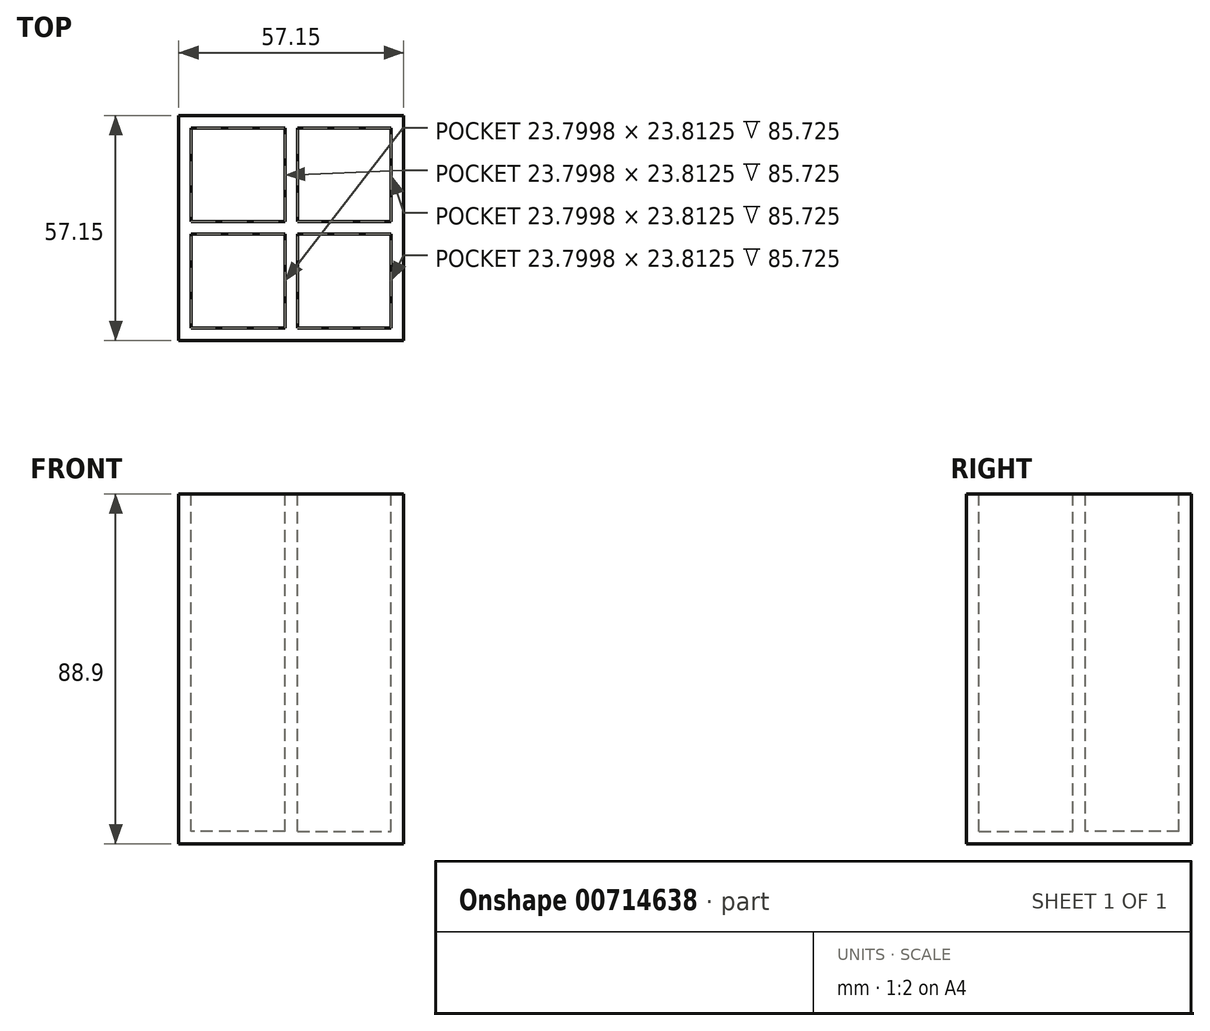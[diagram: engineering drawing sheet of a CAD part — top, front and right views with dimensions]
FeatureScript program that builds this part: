
annotation { "Feature Type Name" : "Feature", "Feature Type Description" : "" }
export const myFeature = defineFeature(function(context is Context, id is Id, definition is map)
    precondition{}
    {
        {
            var Q0;
            Q0=qCreatedBy(makeId("Top.planeOp"),FACE);
            var sketch = newSketch(context, id + "F0", { "sketchPlane" : qUnion([Q0])});
            skLineSegment(sketch, "E0.bottom", {"start": v(-54.12, 72.6) * mm, "end": v(3.03, 72.6) * mm});
            skLineSegment(sketch, "E0.top", {"start": v(-54.12, 15.45) * mm, "end": v(3.03, 15.45) * mm});
            skLineSegment(sketch, "E0.left", {"start": v(-54.12, 72.6) * mm, "end": v(-54.12, 15.45) * mm});
            skLineSegment(sketch, "E0.right", {"start": v(3.03, 72.6) * mm, "end": v(3.03, 15.45) * mm});
            skSolve(sketch);
        }
        {
            var Q0;
            Q0=makeQuery(id+"F0.imprint","IMPRINT",FACE,{"disambiguationData":[TD([[makeQuery(id+"F0.imprint","IMPRINT",EDGE,{"derivedFrom":sQuery(id+"F0.wireOp",EDGE,"E0.bottom")}),-1.0]])]});
            extrude(context, id + "F1", {"entities" : qUnion([Q0]), "depth" : 88.9 * mm, "offsetDistance" : 25.4 * mm});
        }
        {
            var Q0;
            Q0=makeQuery(id+"F1.opExtrude","CAP_FACE",FACE,{"disambiguationData":[OSD([sQuery(id+"F0.wireOp",EDGE,"E0.bottom"),sQuery(id+"F0.wireOp",EDGE,"E0.top"),sQuery(id+"F0.wireOp",EDGE,"E0.left"),sQuery(id+"F0.wireOp",EDGE,"E0.right")])],"isStart":false});
            var sketch = newSketch(context, id + "F2", { "sketchPlane" : qUnion([Q0])});
            skLineSegment(sketch, "E1", {"start": v(-25.54, 72.6) * mm, "end": v(-25.54, 15.45) * mm});
            skLineSegment(sketch, "E2", {"start": v(-54.12, 44.03) * mm, "end": v(3.03, 44.03) * mm});
            skLineSegment(sketch, "E3", {"start": v(-54.12, 45.61) * mm, "end": v(3.03, 45.61) * mm});
            skLineSegment(sketch, "E4", {"start": v(3.03, 42.44) * mm, "end": v(-54.12, 42.44) * mm});
            skLineSegment(sketch, "E5", {"start": v(-54.12, 18.63) * mm, "end": v(3.03, 18.63) * mm});
            skLineSegment(sketch, "E6", {"start": v(-54.12, 69.43) * mm, "end": v(3.03, 69.43) * mm});
            skLineSegment(sketch, "E7", {"start": v(-50.94, 72.6) * mm, "end": v(-50.94, 15.45) * mm});
            skLineSegment(sketch, "E8", {"start": v(-0.14, 72.6) * mm, "end": v(-0.14, 15.45) * mm});
            skLineSegment(sketch, "E9", {"start": v(-23.94, 15.45) * mm, "end": v(-23.94, 72.6) * mm});
            skLineSegment(sketch, "E10", {"start": v(-27.14, 15.45) * mm, "end": v(-27.14, 72.6) * mm});
            skSolve(sketch);
        }
        {
            var Q0;
            {var subQ0=sQuery(id+"F2.wireOp",EDGE,"E10");var subQ1=sQuery(id+"F2.wireOp",EDGE,"E4");var subQ2=makeQuery(id+"F2.imprint","INTERSECT",VERTEX,{"derivedFrom":[subQ1,subQ0]});Q0=makeQuery(id+"F2.imprint","IMPRINT",FACE,{"disambiguationData":[TD([[makeQuery(id+"F2.imprint","IMPRINT",EDGE,{"disambiguationData":[TD([[subQ2,-1.0]])],"derivedFrom":subQ1}),1.0]])]});}
            var Q1;
            {var subQ0=sQuery(id+"F2.wireOp",EDGE,"E7");var subQ1=sQuery(id+"F2.wireOp",EDGE,"E3");var subQ2=makeQuery(id+"F2.imprint","INTERSECT",VERTEX,{"derivedFrom":[subQ1,subQ0]});Q1=makeQuery(id+"F2.imprint","IMPRINT",FACE,{"disambiguationData":[TD([[makeQuery(id+"F2.imprint","IMPRINT",EDGE,{"disambiguationData":[TD([[subQ2,-1.0]])],"derivedFrom":subQ1}),1.0]])]});}
            var Q2;
            {var subQ0=sQuery(id+"F2.wireOp",EDGE,"E9");var subQ1=sQuery(id+"F2.wireOp",EDGE,"E3");var subQ2=makeQuery(id+"F2.imprint","INTERSECT",VERTEX,{"derivedFrom":[subQ1,subQ0]});Q2=makeQuery(id+"F2.imprint","IMPRINT",FACE,{"disambiguationData":[TD([[makeQuery(id+"F2.imprint","IMPRINT",EDGE,{"disambiguationData":[TD([[subQ2,-1.0]])],"derivedFrom":subQ1}),1.0]])]});}
            var Q3;
            {var subQ0=sQuery(id+"F2.wireOp",EDGE,"E8");var subQ1=sQuery(id+"F2.wireOp",EDGE,"E4");var subQ2=makeQuery(id+"F2.imprint","INTERSECT",VERTEX,{"derivedFrom":[subQ1,subQ0]});Q3=makeQuery(id+"F2.imprint","IMPRINT",FACE,{"disambiguationData":[TD([[makeQuery(id+"F2.imprint","IMPRINT",EDGE,{"disambiguationData":[TD([[subQ2,-1.0]])],"derivedFrom":subQ1}),1.0]])]});}
            extrude(context, id + "F3", {"entities" : qUnion([Q0, Q1, Q2, Q3]), "operationType" : NewBodyOperationType.REMOVE, "oppositeDirection" : true, "depth" : 85.72 * mm, "offsetDistance" : 25.4 * mm});
        }
    });
